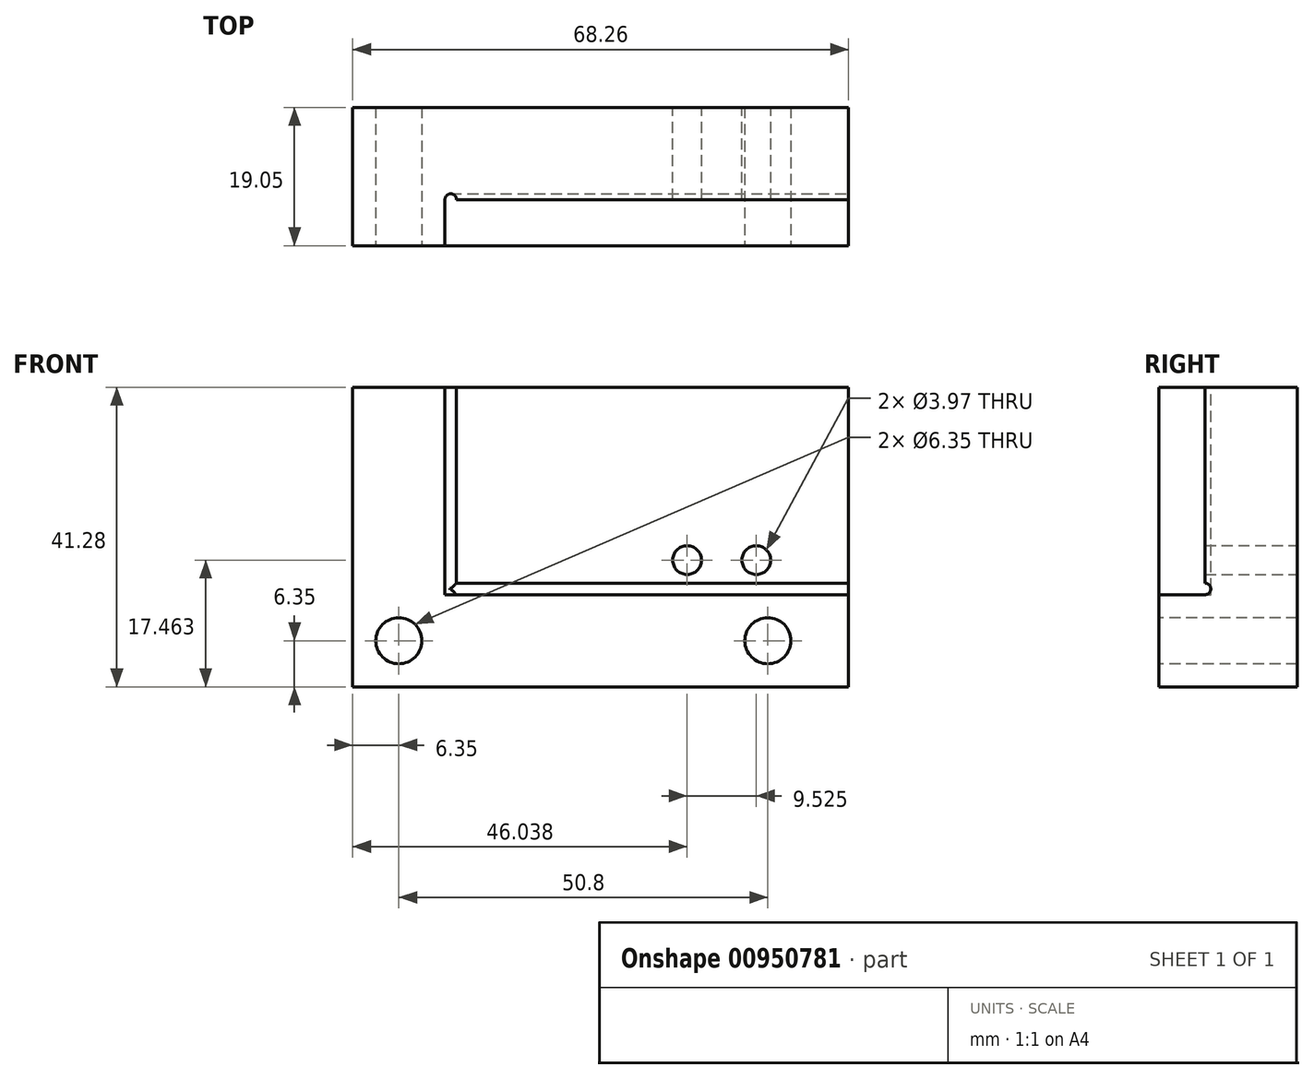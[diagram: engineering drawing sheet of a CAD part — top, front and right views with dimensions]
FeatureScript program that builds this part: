
annotation { "Feature Type Name" : "Feature", "Feature Type Description" : "" }
export const myFeature = defineFeature(function(context is Context, id is Id, definition is map)
    precondition{}
    {
        {
            var Q0;
            Q0=qCreatedBy(makeId("Front.planeOp"),FACE);
            var sketch = newSketch(context, id + "F0", { "sketchPlane" : qUnion([Q0])});
            skPoint(sketch, "E0", {"position": v(14.29, -12.98) * mm});
            skCircle(sketch, "E1", {"center": v(14.29, -12.98) * mm, "radius": 1.98 * mm});
            skLineSegment(sketch, "E2", {"start": v(-19.05, 10.84) * mm, "end": v(-19.05, -17.74) * mm});
            skPoint(sketch, "E3", {"position": v(23.81, -12.98) * mm});
            skCircle(sketch, "E4", {"center": v(23.81, -12.98) * mm, "radius": 1.98 * mm});
            skLineSegment(sketch, "E5.bottom", {"start": v(-31.75, -30.44) * mm, "end": v(36.51, -30.44) * mm});
            skLineSegment(sketch, "E5.top", {"start": v(-31.75, 10.84) * mm, "end": v(36.51, 10.84) * mm});
            skLineSegment(sketch, "E5.left", {"start": v(-31.75, -30.44) * mm, "end": v(-31.75, 10.84) * mm});
            skLineSegment(sketch, "E5.right", {"start": v(36.51, -30.44) * mm, "end": v(36.51, 10.84) * mm});
            skLineSegment(sketch, "E6", {"start": v(-19.05, -17.74) * mm, "end": v(36.51, -17.74) * mm});
            skSolve(sketch);
        }
        {
            var Q0;
            {var subQ10=sQuery(id+"F0.wireOp",EDGE,"E2");Q0=makeQuery(id+"F0.imprint","IMPRINT",FACE,{"disambiguationData":[TD([[makeQuery(id+"F0.imprint","IMPRINT",EDGE,{"derivedFrom":subQ10}),-1.0]])]});}
            var Q1;
            {var subQ13=sQuery(id+"F0.wireOp",EDGE,"E2");Q1=makeQuery(id+"F0.imprint","IMPRINT",FACE,{"disambiguationData":[TD([[makeQuery(id+"F0.imprint","IMPRINT",EDGE,{"derivedFrom":subQ13}),1.0]])]});}
            var Q2;
            {var subQ0=sQuery(id+"F0.wireOp",EDGE,"e0abeeca-aecd-4282-884a-1ba8039fda41");var subQ1=sQuery(id+"F0.wireOp",EDGE,"bf459676-9bbd-49e1-ab9e-19eefacaccf8");var subQ2=makeQuery(id+"F0.imprint","INTERSECT",VERTEX,{"derivedFrom":[subQ1,subQ0]});Q2=makeQuery(id+"F0.imprint","IMPRINT",FACE,{"disambiguationData":[TD([[makeQuery(id+"F0.imprint","IMPRINT",EDGE,{"disambiguationData":[TD([[subQ2,1.0]])],"derivedFrom":subQ1}),1.0]])]});}
            extrude(context, id + "F1", {"entities" : qUnion([Q0, Q1, Q2]), "depth" : 19.05 * mm, "offsetDistance" : 25.4 * mm});
        }
        {
            var Q0;
            Q0=makeQuery(id+"F1.opExtrude","CAP_FACE",FACE,{"disambiguationData":[OSD([sQuery(id+"F0.wireOp",EDGE,"b041aa4c-38af-473a-b6d1-90a53f403c20"),sQuery(id+"F0.wireOp",EDGE,"e0abeeca-aecd-4282-884a-1ba8039fda41"),sQuery(id+"F0.wireOp",EDGE,"3b4b963a-9766-4dd1-8c4d-700a4368aff9"),sQuery(id+"F0.wireOp",EDGE,"E1"),sQuery(id+"F0.wireOp",EDGE,"E4"),sQuery(id+"F0.wireOp",EDGE,"E5.bottom"),sQuery(id+"F0.wireOp",EDGE,"E5.top"),sQuery(id+"F0.wireOp",EDGE,"E5.left"),sQuery(id+"F0.wireOp",EDGE,"E5.right")])],"isStart":false});
            var sketch = newSketch(context, id + "F2", { "sketchPlane" : qUnion([Q0])});
            skLineSegment(sketch, "E7.bottom", {"start": v(-19.05, 10.84) * mm, "end": v(36.51, 10.84) * mm});
            skLineSegment(sketch, "E7.top", {"start": v(-19.05, -17.74) * mm, "end": v(36.51, -17.74) * mm});
            skLineSegment(sketch, "E7.left", {"start": v(-19.05, 10.84) * mm, "end": v(-19.05, -17.74) * mm});
            skLineSegment(sketch, "E7.right", {"start": v(36.51, 10.84) * mm, "end": v(36.51, -17.74) * mm});
            skLineSegment(sketch, "E8", {"start": v(-31.75, -30.44) * mm, "end": v(-31.75, -24.09) * mm});
            skLineSegment(sketch, "E9", {"start": v(-31.75, -24.09) * mm, "end": v(-25.4, -24.09) * mm});
            skPoint(sketch, "E10", {"position": v(-25.4, -24.09) * mm});
            skLineSegment(sketch, "E11", {"start": v(36.51, -30.44) * mm, "end": v(36.51, -24.09) * mm});
            skLineSegment(sketch, "E12", {"start": v(36.51, -24.09) * mm, "end": v(25.4, -24.09) * mm});
            skPoint(sketch, "E13", {"position": v(25.4, -24.09) * mm});
            skLineSegment(sketch, "E14", {"start": v(-31.75, -30.44) * mm, "end": v(-31.75, -27.26) * mm});
            skLineSegment(sketch, "E15", {"start": v(-31.75, -27.26) * mm, "end": v(42.3, -27.26) * mm});
            skCircle(sketch, "E16", {"center": v(-25.4, -24.09) * mm, "radius": 3.18 * mm});
            skCircle(sketch, "E17", {"center": v(25.4, -24.09) * mm, "radius": 3.18 * mm});
            skSolve(sketch);
        }
        {
            var Q0;
            Q0=makeQuery(id+"F2.imprint","IMPRINT",FACE,{"disambiguationData":[TD([[makeQuery(id+"F2.imprint","IMPRINT",EDGE,{"derivedFrom":sQuery(id+"F2.wireOp",EDGE,"E7.bottom")}),-1.0]])]});
            extrude(context, id + "F3", {"entities" : qUnion([Q0]), "operationType" : NewBodyOperationType.REMOVE, "oppositeDirection" : true, "depth" : 6.35 * mm, "offsetDistance" : 25.4 * mm});
        }
        {
            var Q0;
            Q0=sQuery(id+"F2.wireOp",VERTEX,"E9.end");
            var Q1;
            Q1=sQuery(id+"F2.wireOp",VERTEX,"E12.end");
            var Q2;
            Q2=makeQuery(id+"F1.opExtrude","SWEPT_BODY",BODY,{"disambiguationData":[OSD([sQuery(id+"F0.wireOp",EDGE,"b041aa4c-38af-473a-b6d1-90a53f403c20"),sQuery(id+"F0.wireOp",EDGE,"e0abeeca-aecd-4282-884a-1ba8039fda41"),sQuery(id+"F0.wireOp",EDGE,"3b4b963a-9766-4dd1-8c4d-700a4368aff9"),sQuery(id+"F0.wireOp",EDGE,"E1"),sQuery(id+"F0.wireOp",EDGE,"E4"),sQuery(id+"F0.wireOp",EDGE,"E5.bottom"),sQuery(id+"F0.wireOp",EDGE,"E5.top"),sQuery(id+"F0.wireOp",EDGE,"E5.left"),sQuery(id+"F0.wireOp",EDGE,"E5.right")])]});
            hole(context, id + "F4", {"style" : HoleStyle.SIMPLE, "endStyle" : HoleEndStyle.THROUGH, "holeDiameter" : 6.35 * mm, "majorDiameter" : 6.35 * mm, "isTappedThrough" : true, "tappedDepth" : 12.7 * mm, "tapClearance" : 3, "startFromSketch" : true, "locations" : qUnion([Q0, Q1]), "scope" : qUnion([Q2])});
        }
        {
            var Q0;
            Q0=makeQuery(id+"F1.opExtrude","SWEPT_FACE",FACE,{"disambiguationData":[OSD([sQuery(id+"F0.wireOp",EDGE,"E5.top")])]});
            var sketch = newSketch(context, id + "F5", { "sketchPlane" : qUnion([Q0])});
            skPoint(sketch, "E18", {"position": v(-18.26, -12.7) * mm});
            skCircle(sketch, "E19", {"center": v(-18.26, -12.7) * mm, "radius": 0.8 * mm});
            skSolve(sketch);
        }
        {
            var Q0;
            Q0 = qSketchRegion(id + "F5", true);
            var Q1;
            {var subQ0=sQuery(id+"F5.wireOp",EDGE,"E19");var subQ1=sQuery(id+"F2.wireOp",EDGE,"E7.bottom");var subQ2=makeQuery(id+"F3.boolean.opBoolean","COPY",EDGE,{"derivedFrom":makeQuery(id+"F3.opExtrude","CAP_EDGE",EDGE,{"disambiguationData":[OSD([subQ1])],"isStart":false})});var subQ4=makeQuery(id+"F5.imprint","INTERSECT",VERTEX,{"derivedFrom":[subQ2,subQ0]});Q1=makeQuery(id+"F5.imprint","IMPRINT",FACE,{"disambiguationData":[TD([[makeQuery(id+"F5.imprint","IMPRINT",EDGE,{"disambiguationData":[TD([[subQ4,-1.0]])],"derivedFrom":subQ0}),1.0]])]});}
            extrude(context, id + "F6", {"entities" : qUnion([Q0, Q1]), "operationType" : NewBodyOperationType.REMOVE, "oppositeDirection" : true, "depth" : 28.57 * mm, "offsetDistance" : 25.4 * mm});
        }
        {
            var Q0;
            Q0=makeQuery(id+"F1.opExtrude","SWEPT_FACE",FACE,{"disambiguationData":[OSD([sQuery(id+"F0.wireOp",EDGE,"E5.right")])]});
            var sketch = newSketch(context, id + "F7", { "sketchPlane" : qUnion([Q0])});
            skPoint(sketch, "E20", {"position": v(-12.7, -16.95) * mm});
            skCircle(sketch, "E21", {"center": v(-12.7, -16.95) * mm, "radius": 0.8 * mm});
            skSolve(sketch);
        }
        {
            var Q0;
            {var subQ0=sQuery(id+"F7.wireOp",EDGE,"E21");var subQ1=sQuery(id+"F2.wireOp",EDGE,"E7.right");var subQ2=makeQuery(id+"F3.boolean.opBoolean","COPY",EDGE,{"derivedFrom":makeQuery(id+"F3.opExtrude","CAP_EDGE",EDGE,{"disambiguationData":[OSD([subQ1])],"isStart":false})});var subQ4=makeQuery(id+"F7.imprint","INTERSECT",VERTEX,{"derivedFrom":[subQ2,subQ0]});Q0=makeQuery(id+"F7.imprint","IMPRINT",FACE,{"disambiguationData":[TD([[makeQuery(id+"F7.imprint","IMPRINT",EDGE,{"disambiguationData":[TD([[subQ4,1.0]])],"derivedFrom":subQ0}),1.0]])]});}
            extrude(context, id + "F8", {"entities" : qUnion([Q0]), "operationType" : NewBodyOperationType.REMOVE, "oppositeDirection" : true, "depth" : 54.86 * mm, "offsetDistance" : 25.4 * mm});
        }
    });
